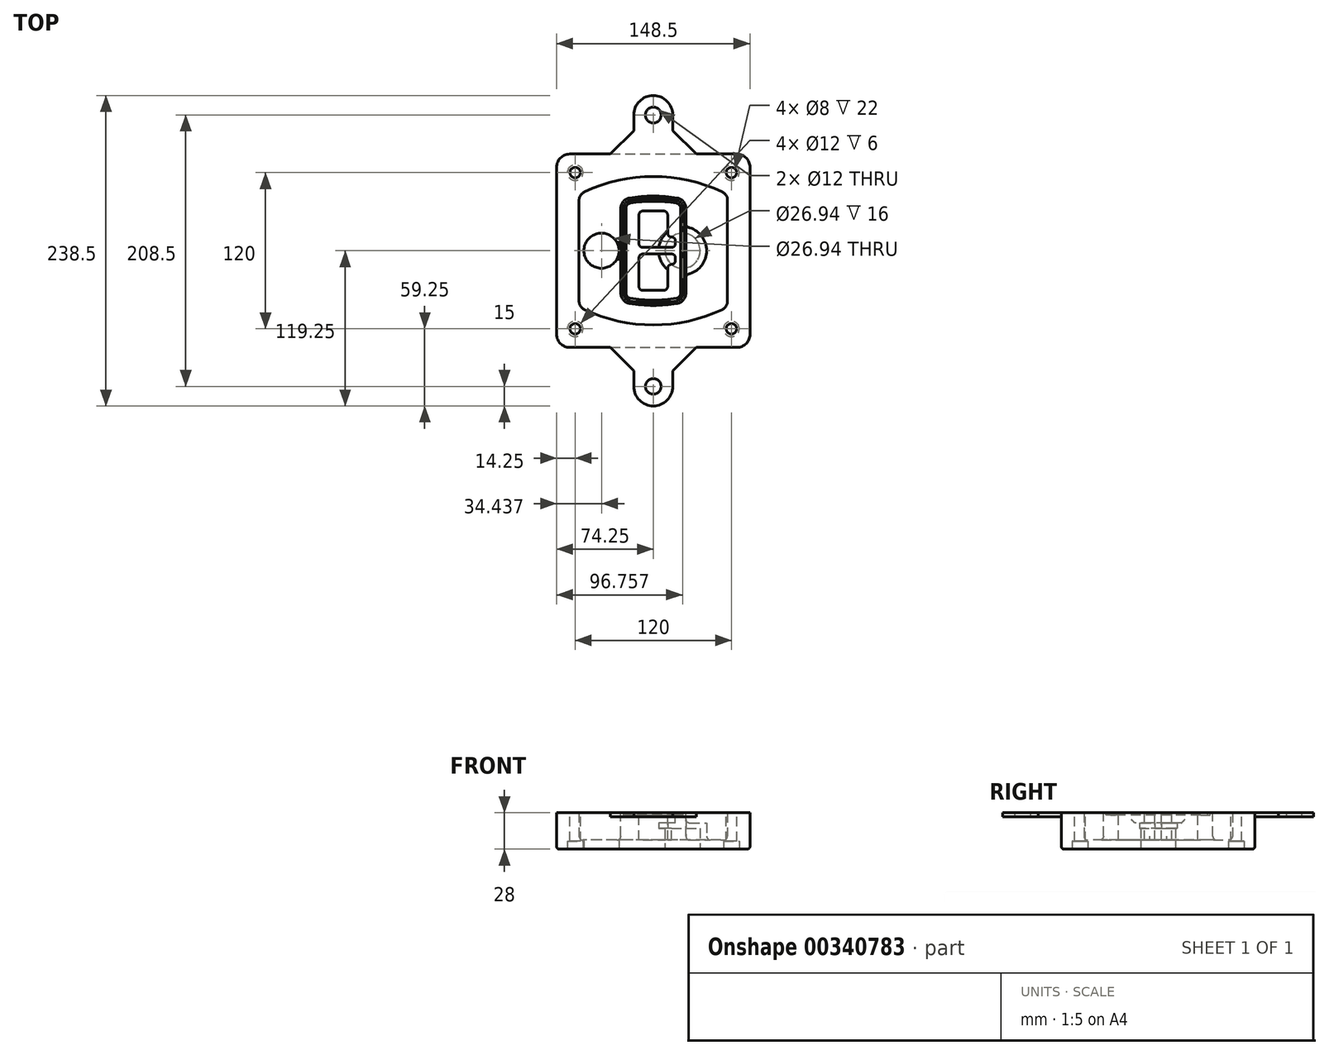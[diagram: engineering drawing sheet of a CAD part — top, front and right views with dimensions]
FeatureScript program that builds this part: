
annotation { "Feature Type Name" : "Feature", "Feature Type Description" : "" }
export const myFeature = defineFeature(function(context is Context, id is Id, definition is map)
    precondition{}
    {
        {
            var Q0;
            Q0=qCreatedBy(makeId("Top.planeOp"),FACE);
            var sketch = newSketch(context, id + "F0", { "sketchPlane" : qUnion([Q0])});
            skPoint(sketch, "E0.rect.middle", {"position": v(0, 0) * mm});
            skLineSegment(sketch, "E1.bottom", {"start": v(-64.25, -74.25) * mm, "end": v(64.25, -74.25) * mm});
            skLineSegment(sketch, "E1.top", {"start": v(-64.25, 74.25) * mm, "end": v(64.25, 74.25) * mm});
            skLineSegment(sketch, "E1.left", {"start": v(-74.25, -64.25) * mm, "end": v(-74.25, 64.25) * mm});
            skLineSegment(sketch, "E1.right", {"start": v(74.25, -64.25) * mm, "end": v(74.25, 64.25) * mm});
            skLineSegment(sketch, "E2", {"start": v(-74.25, 74.25) * mm, "end": v(74.25, -74.25) * mm, "construction": true});
            skLineSegment(sketch, "E3", {"start": v(74.25, 74.25) * mm, "end": v(-74.25, -74.25) * mm, "construction": true});
            skCircle(sketch, "E4", {"center": v(-60, 60) * mm, "radius": 4 * mm});
            skCircle(sketch, "E5", {"center": v(60, 60) * mm, "radius": 4 * mm});
            skCircle(sketch, "E6", {"center": v(60, -60) * mm, "radius": 4 * mm});
            skCircle(sketch, "E7", {"center": v(-60, -60) * mm, "radius": 4 * mm});
            skLineSegment(sketch, "E8", {"start": v(-60, 60) * mm, "end": v(60, 60) * mm, "construction": true});
            skLineSegment(sketch, "E9", {"start": v(60, 60) * mm, "end": v(60, -60) * mm, "construction": true});
            skLineSegment(sketch, "E10", {"start": v(60, -60) * mm, "end": v(-60, -60) * mm, "construction": true});
            skLineSegment(sketch, "E11", {"start": v(-60, -60) * mm, "end": v(-60, 60) * mm, "construction": true});
            skLineSegment(sketch, "E12", {"start": v(-60, 38.83) * mm, "end": v(-60, -38.83) * mm});
            skLineSegment(sketch, "E13", {"start": v(60, 38.83) * mm, "end": v(60, -38.83) * mm});
            skArc(sketch, "E14", {"start": v(54.26, 47.88) * mm, "mid": v(0, 60) * mm, "end": v(-54.26, 47.88) * mm});
            skArc(sketch, "E15", {"start": v(-54.26, -47.88) * mm, "mid": v(0, -60) * mm, "end": v(54.26, -47.88) * mm});
            skLineSegment(sketch, "E16", {"start": v(-60, 0) * mm, "end": v(60, 0) * mm, "construction": true});
            skPoint(sketch, "E17.visualSharp", {"position": v(-60, -45) * mm});
            skArc(sketch, "E17.filletArc", {"start": v(-60, -38.83) * mm, "mid": v(-58.44, -44.2) * mm, "end": v(-54.26, -47.88) * mm});
            skPoint(sketch, "E18.visualSharp", {"position": v(-60, 45) * mm});
            skArc(sketch, "E18.filletArc", {"start": v(-54.26, 47.88) * mm, "mid": v(-58.44, 44.2) * mm, "end": v(-60, 38.83) * mm});
            skPoint(sketch, "E19.visualSharp", {"position": v(60, 45) * mm});
            skArc(sketch, "E19.filletArc", {"start": v(60, 38.83) * mm, "mid": v(58.44, 44.2) * mm, "end": v(54.26, 47.88) * mm});
            skPoint(sketch, "E20.visualSharp", {"position": v(60, -45) * mm});
            skArc(sketch, "E20.filletArc", {"start": v(54.26, -47.88) * mm, "mid": v(58.44, -44.2) * mm, "end": v(60, -38.83) * mm});
            skPoint(sketch, "E21.visualSharp", {"position": v(-74.25, 74.25) * mm});
            skArc(sketch, "E21.filletArc", {"start": v(-64.25, 74.25) * mm, "mid": v(-71.32, 71.32) * mm, "end": v(-74.25, 64.25) * mm});
            skPoint(sketch, "E22.visualSharp", {"position": v(74.25, 74.25) * mm});
            skArc(sketch, "E22.filletArc", {"start": v(74.25, 64.25) * mm, "mid": v(71.32, 71.32) * mm, "end": v(64.25, 74.25) * mm});
            skPoint(sketch, "E23.visualSharp", {"position": v(74.25, -74.25) * mm});
            skArc(sketch, "E23.filletArc", {"start": v(64.25, -74.25) * mm, "mid": v(71.32, -71.32) * mm, "end": v(74.25, -64.25) * mm});
            skPoint(sketch, "E24.visualSharp", {"position": v(-74.25, -74.25) * mm});
            skArc(sketch, "E24.filletArc", {"start": v(-74.25, -64.25) * mm, "mid": v(-71.32, -71.32) * mm, "end": v(-64.25, -74.25) * mm});
            skArc(sketch, "E25.0", {"start": v(57, 38.83) * mm, "mid": v(55.9, 42.58) * mm, "end": v(52.98, 45.17) * mm});
            skLineSegment(sketch, "E25.1", {"start": v(57, 38.83) * mm, "end": v(57, -38.83) * mm});
            skArc(sketch, "E25.2", {"start": v(52.98, -45.17) * mm, "mid": v(55.9, -42.58) * mm, "end": v(57, -38.83) * mm});
            skArc(sketch, "E25.3", {"start": v(-52.98, -45.17) * mm, "mid": v(0, -57) * mm, "end": v(52.98, -45.17) * mm});
            skArc(sketch, "E25.4", {"start": v(-57, -38.83) * mm, "mid": v(-55.9, -42.58) * mm, "end": v(-52.98, -45.17) * mm});
            skArc(sketch, "E25.5", {"start": v(52.98, 45.17) * mm, "mid": v(0, 57) * mm, "end": v(-52.98, 45.17) * mm});
            skLineSegment(sketch, "E25.6", {"start": v(-57, 38.83) * mm, "end": v(-57, -38.83) * mm});
            skArc(sketch, "E25.7", {"start": v(-52.98, 45.17) * mm, "mid": v(-55.9, 42.58) * mm, "end": v(-57, 38.83) * mm});
            skArc(sketch, "E26.0", {"start": v(-55.96, 51.5) * mm, "mid": v(-61.82, 46.33) * mm, "end": v(-64, 38.83) * mm});
            skArc(sketch, "E26.1", {"start": v(55.96, 51.5) * mm, "mid": v(0, 64) * mm, "end": v(-55.96, 51.5) * mm});
            skArc(sketch, "E26.2", {"start": v(64, 38.83) * mm, "mid": v(61.82, 46.33) * mm, "end": v(55.96, 51.5) * mm});
            skLineSegment(sketch, "E26.3", {"start": v(64, 38.83) * mm, "end": v(64, -38.83) * mm});
            skArc(sketch, "E26.4", {"start": v(55.96, -51.5) * mm, "mid": v(61.82, -46.33) * mm, "end": v(64, -38.83) * mm});
            skLineSegment(sketch, "E26.5", {"start": v(-64, 38.83) * mm, "end": v(-64, -38.83) * mm});
            skArc(sketch, "E26.6", {"start": v(-55.96, -51.5) * mm, "mid": v(0, -64) * mm, "end": v(55.96, -51.5) * mm});
            skArc(sketch, "E26.7", {"start": v(-64, -38.83) * mm, "mid": v(-61.82, -46.33) * mm, "end": v(-55.96, -51.5) * mm});
            skSolve(sketch);
        }
        {
            var Q0;
            Q0=makeQuery(id+"F0.imprint","IMPRINT",FACE,{"disambiguationData":[TD([[makeQuery(id+"F0.imprint","IMPRINT",EDGE,{"derivedFrom":sQuery(id+"F0.wireOp",EDGE,"E1.bottom")}),1.0]])]});
            var Q1;
            Q1=makeQuery(id+"F0.imprint","IMPRINT",FACE,{"disambiguationData":[TD([[makeQuery(id+"F0.imprint","IMPRINT",EDGE,{"derivedFrom":sQuery(id+"F0.wireOp",EDGE,"E12")}),1.0]])]});
            var Q2;
            Q2=makeQuery(id+"F0.imprint","IMPRINT",FACE,{"disambiguationData":[TD([[makeQuery(id+"F0.imprint","IMPRINT",EDGE,{"derivedFrom":sQuery(id+"F0.wireOp",EDGE,"E25.0")}),1.0]])]});
            var Q3;
            Q3=makeQuery(id+"F0.imprint","IMPRINT",FACE,{"disambiguationData":[TD([[makeQuery(id+"F0.imprint","IMPRINT",EDGE,{"derivedFrom":sQuery(id+"F0.wireOp",EDGE,"E12")}),-1.0]])]});
            extrude(context, id + "F1", {"entities" : qUnion([Q0, Q1, Q2, Q3]), "oppositeDirection" : true, "depth" : 25 * mm});
        }
        {
            var Q0;
            Q0=makeQuery(id+"F0.imprint","IMPRINT",FACE,{"disambiguationData":[TD([[makeQuery(id+"F0.imprint","IMPRINT",EDGE,{"derivedFrom":sQuery(id+"F0.wireOp",EDGE,"E12")}),1.0]])]});
            extrude(context, id + "F2", {"entities" : qUnion([Q0]), "operationType" : NewBodyOperationType.ADD, "depth" : 3 * mm});
        }
        {
            var Q0;
            Q0=makeQuery(id+"F0.imprint","IMPRINT",FACE,{"disambiguationData":[TD([[makeQuery(id+"F0.imprint","IMPRINT",EDGE,{"derivedFrom":sQuery(id+"F0.wireOp",EDGE,"E25.0")}),1.0]])]});
            extrude(context, id + "F3", {"entities" : qUnion([Q0]), "operationType" : NewBodyOperationType.REMOVE, "oppositeDirection" : true, "depth" : 18 * mm});
        }
        {
            var Q0;
            Q0=makeQuery(id+"F2.opExtrude","CAP_FACE",FACE,{"disambiguationData":[OSD([sQuery(id+"F0.wireOp",EDGE,"E12"),sQuery(id+"F0.wireOp",EDGE,"E13"),sQuery(id+"F0.wireOp",EDGE,"E14"),sQuery(id+"F0.wireOp",EDGE,"E15"),sQuery(id+"F0.wireOp",EDGE,"E17.filletArc"),sQuery(id+"F0.wireOp",EDGE,"E18.filletArc"),sQuery(id+"F0.wireOp",EDGE,"E19.filletArc"),sQuery(id+"F0.wireOp",EDGE,"E20.filletArc"),sQuery(id+"F0.wireOp",EDGE,"E25.0"),sQuery(id+"F0.wireOp",EDGE,"E25.1"),sQuery(id+"F0.wireOp",EDGE,"E25.2"),sQuery(id+"F0.wireOp",EDGE,"E25.3"),sQuery(id+"F0.wireOp",EDGE,"E25.4"),sQuery(id+"F0.wireOp",EDGE,"E25.5"),sQuery(id+"F0.wireOp",EDGE,"E25.6"),sQuery(id+"F0.wireOp",EDGE,"E25.7")])],"isStart":false});
            var sketch = newSketch(context, id + "F4", { "sketchPlane" : qUnion([Q0])});
            skArc(sketch, "E27.0", {"start": v(-18.34, -40.45) * mm, "mid": v(0, -42) * mm, "end": v(18.34, -40.45) * mm});
            skArc(sketch, "E28.0", {"start": v(18.34, 40.45) * mm, "mid": v(0, 42) * mm, "end": v(-18.34, 40.45) * mm});
            skLineSegment(sketch, "E29", {"start": v(-25, 32.57) * mm, "end": v(-25, -32.57) * mm});
            skLineSegment(sketch, "E30", {"start": v(25, 32.57) * mm, "end": v(25, -32.57) * mm});
            skLineSegment(sketch, "E31", {"start": v(-25, 39.1) * mm, "end": v(25, 39.1) * mm, "construction": true});
            skLineSegment(sketch, "E32", {"start": v(-25, -39.1) * mm, "end": v(25, -39.1) * mm, "construction": true});
            skPoint(sketch, "E33.visualSharp", {"position": v(-25, 39.1) * mm});
            skArc(sketch, "E33.filletArc", {"start": v(-18.34, 40.45) * mm, "mid": v(-23.11, 37.73) * mm, "end": v(-25, 32.57) * mm});
            skPoint(sketch, "E34.visualSharp", {"position": v(25, 39.1) * mm});
            skArc(sketch, "E34.filletArc", {"start": v(25, 32.57) * mm, "mid": v(23.11, 37.73) * mm, "end": v(18.34, 40.45) * mm});
            skPoint(sketch, "E35.visualSharp", {"position": v(25, -39.1) * mm});
            skArc(sketch, "E35.filletArc", {"start": v(18.34, -40.45) * mm, "mid": v(23.11, -37.73) * mm, "end": v(25, -32.57) * mm});
            skPoint(sketch, "E36.visualSharp", {"position": v(-25, -39.1) * mm});
            skArc(sketch, "E36.filletArc", {"start": v(-25, -32.57) * mm, "mid": v(-23.11, -37.73) * mm, "end": v(-18.34, -40.45) * mm});
            skArc(sketch, "E37.0", {"start": v(52.98, 45.17) * mm, "mid": v(0, 57) * mm, "end": v(-52.98, 45.17) * mm});
            skArc(sketch, "E37.1", {"start": v(-52.98, 45.17) * mm, "mid": v(-55.9, 42.58) * mm, "end": v(-57, 38.83) * mm});
            skLineSegment(sketch, "E37.2", {"start": v(-57, 38.83) * mm, "end": v(-57, -38.83) * mm});
            skArc(sketch, "E37.3", {"start": v(-57, -38.83) * mm, "mid": v(-55.9, -42.58) * mm, "end": v(-52.98, -45.17) * mm});
            skArc(sketch, "E37.4", {"start": v(-52.98, -45.17) * mm, "mid": v(0, -57) * mm, "end": v(52.98, -45.17) * mm});
            skArc(sketch, "E37.5", {"start": v(52.98, -45.17) * mm, "mid": v(55.9, -42.58) * mm, "end": v(57, -38.83) * mm});
            skLineSegment(sketch, "E37.6", {"start": v(57, 38.83) * mm, "end": v(57, -38.83) * mm});
            skArc(sketch, "E37.7", {"start": v(57, 38.83) * mm, "mid": v(55.9, 42.58) * mm, "end": v(52.98, 45.17) * mm});
            skLineSegment(sketch, "E38.0", {"start": v(23, 32.57) * mm, "end": v(23, -32.57) * mm});
            skArc(sketch, "E38.1", {"start": v(18, -38.48) * mm, "mid": v(21.58, -36.44) * mm, "end": v(23, -32.57) * mm});
            skArc(sketch, "E38.2", {"start": v(-18, -38.48) * mm, "mid": v(0, -40) * mm, "end": v(18, -38.48) * mm});
            skArc(sketch, "E38.3", {"start": v(-23, -32.57) * mm, "mid": v(-21.58, -36.44) * mm, "end": v(-18, -38.48) * mm});
            skLineSegment(sketch, "E38.4", {"start": v(-23, 32.57) * mm, "end": v(-23, -32.57) * mm});
            skArc(sketch, "E38.5", {"start": v(23, 32.57) * mm, "mid": v(21.58, 36.44) * mm, "end": v(18, 38.48) * mm});
            skArc(sketch, "E38.6", {"start": v(-18, 38.48) * mm, "mid": v(-21.58, 36.44) * mm, "end": v(-23, 32.57) * mm});
            skArc(sketch, "E38.7", {"start": v(18, 38.48) * mm, "mid": v(0, 40) * mm, "end": v(-18, 38.48) * mm});
            skArc(sketch, "E39.0", {"start": v(21, 32.57) * mm, "mid": v(20.06, 35.15) * mm, "end": v(17.67, 36.5) * mm});
            skLineSegment(sketch, "E39.1", {"start": v(21, 32.57) * mm, "end": v(21, -32.57) * mm});
            skArc(sketch, "E39.2", {"start": v(17.67, -36.5) * mm, "mid": v(20.06, -35.15) * mm, "end": v(21, -32.57) * mm});
            skArc(sketch, "E39.3", {"start": v(-17.67, -36.5) * mm, "mid": v(0, -38) * mm, "end": v(17.67, -36.5) * mm});
            skArc(sketch, "E39.4", {"start": v(-21, -32.57) * mm, "mid": v(-20.06, -35.15) * mm, "end": v(-17.67, -36.5) * mm});
            skArc(sketch, "E39.5", {"start": v(17.67, 36.5) * mm, "mid": v(0, 38) * mm, "end": v(-17.67, 36.5) * mm});
            skLineSegment(sketch, "E39.6", {"start": v(-21, 32.57) * mm, "end": v(-21, -32.57) * mm});
            skArc(sketch, "E39.7", {"start": v(-17.67, 36.5) * mm, "mid": v(-20.06, 35.15) * mm, "end": v(-21, 32.57) * mm});
            skLineSegment(sketch, "E40", {"start": v(-25, 0) * mm, "end": v(25, 0) * mm, "construction": true});
            skLineSegment(sketch, "E41", {"start": v(-11, 5.5) * mm, "end": v(-11, 27.5) * mm});
            skLineSegment(sketch, "E42", {"start": v(-8, 30.5) * mm, "end": v(8, 30.5) * mm});
            skLineSegment(sketch, "E43", {"start": v(11, 27.5) * mm, "end": v(11, 13.5) * mm});
            skLineSegment(sketch, "E44", {"start": v(14, 10.5) * mm, "end": v(14, 10.5) * mm});
            skLineSegment(sketch, "E45", {"start": v(17, 7.5) * mm, "end": v(17, 5.5) * mm});
            skLineSegment(sketch, "E46", {"start": v(14, 2.5) * mm, "end": v(-8, 2.5) * mm});
            skPoint(sketch, "E47.visualSharp", {"position": v(-11, 30.5) * mm});
            skArc(sketch, "E47.filletArc", {"start": v(-8, 30.5) * mm, "mid": v(-10.12, 29.62) * mm, "end": v(-11, 27.5) * mm});
            skPoint(sketch, "E48.visualSharp", {"position": v(11, 30.5) * mm});
            skArc(sketch, "E48.filletArc", {"start": v(11, 27.5) * mm, "mid": v(10.12, 29.62) * mm, "end": v(8, 30.5) * mm});
            skPoint(sketch, "E49.visualSharp", {"position": v(11, 10.5) * mm});
            skArc(sketch, "E49.filletArc", {"start": v(11, 13.5) * mm, "mid": v(11.88, 11.38) * mm, "end": v(14, 10.5) * mm});
            skPoint(sketch, "E50.visualSharp", {"position": v(17, 10.5) * mm});
            skArc(sketch, "E50.filletArc", {"start": v(17, 7.5) * mm, "mid": v(16.12, 9.62) * mm, "end": v(14, 10.5) * mm});
            skPoint(sketch, "E51.visualSharp", {"position": v(17, 2.5) * mm});
            skArc(sketch, "E51.filletArc", {"start": v(14, 2.5) * mm, "mid": v(16.12, 3.38) * mm, "end": v(17, 5.5) * mm});
            skPoint(sketch, "E52.visualSharp", {"position": v(-11, 2.5) * mm});
            skArc(sketch, "E52.filletArc", {"start": v(-11, 5.5) * mm, "mid": v(-10.12, 3.38) * mm, "end": v(-8, 2.5) * mm});
            skLineSegment(sketch, "E53.0.MirrorCS", {"start": v(14, -2.5) * mm, "end": v(-8, -2.5) * mm});
            skArc(sketch, "E54.0.MirrorCS", {"start": v(-11, -5.5) * mm, "mid": v(-10.12, -3.38) * mm, "end": v(-8, -2.5) * mm});
            skLineSegment(sketch, "E55.0.MirrorCS", {"start": v(-11, -5.5) * mm, "end": v(-11, -27.5) * mm});
            skArc(sketch, "E56.0.MirrorCS", {"start": v(-8, -30.5) * mm, "mid": v(-10.12, -29.62) * mm, "end": v(-11, -27.5) * mm});
            skLineSegment(sketch, "E57.0.MirrorCS", {"start": v(-8, -30.5) * mm, "end": v(8, -30.5) * mm});
            skArc(sketch, "E58.0.MirrorCS", {"start": v(11, -27.5) * mm, "mid": v(10.12, -29.62) * mm, "end": v(8, -30.5) * mm});
            skLineSegment(sketch, "E59.0.MirrorCS", {"start": v(11, -27.5) * mm, "end": v(11, -13.5) * mm});
            skArc(sketch, "E60.0.MirrorCS", {"start": v(11, -13.5) * mm, "mid": v(11.88, -11.38) * mm, "end": v(14, -10.5) * mm});
            skArc(sketch, "E61.0.MirrorCS", {"start": v(17, -7.5) * mm, "mid": v(16.12, -9.62) * mm, "end": v(14, -10.5) * mm});
            skLineSegment(sketch, "E62.0.MirrorCS", {"start": v(17, -7.5) * mm, "end": v(17, -5.5) * mm});
            skArc(sketch, "E63.0.MirrorCS", {"start": v(14, -2.5) * mm, "mid": v(16.12, -3.38) * mm, "end": v(17, -5.5) * mm});
            skSolve(sketch);
        }
        {
            var Q0;
            Q0=makeQuery(id+"F4.imprint","IMPRINT",FACE,{"disambiguationData":[TD([[makeQuery(id+"F4.imprint","IMPRINT",EDGE,{"derivedFrom":sQuery(id+"F4.wireOp",EDGE,"E27.0")}),1.0]])]});
            var Q1;
            Q1=makeQuery(id+"F4.imprint","IMPRINT",FACE,{"disambiguationData":[TD([[makeQuery(id+"F4.imprint","IMPRINT",EDGE,{"derivedFrom":sQuery(id+"F4.wireOp",EDGE,"E38.0")}),-1.0]])]});
            var Q2;
            Q2=makeQuery(id+"F4.imprint","IMPRINT",FACE,{"disambiguationData":[TD([[makeQuery(id+"F4.imprint","IMPRINT",EDGE,{"derivedFrom":sQuery(id+"F4.wireOp",EDGE,"E39.0")}),1.0]])]});
            extrude(context, id + "F5", {"entities" : qUnion([Q0, Q1, Q2]), "operationType" : NewBodyOperationType.ADD, "endBound" : BoundingType.UP_TO_NEXT, "oppositeDirection" : true, "depth" : 25 * mm});
        }
        {
            var Q0;
            Q0=makeQuery(id+"F4.imprint","IMPRINT",FACE,{"disambiguationData":[TD([[makeQuery(id+"F4.imprint","IMPRINT",EDGE,{"derivedFrom":sQuery(id+"F4.wireOp",EDGE,"E38.0")}),-1.0]])]});
            extrude(context, id + "F6", {"entities" : qUnion([Q0]), "operationType" : NewBodyOperationType.REMOVE, "oppositeDirection" : true, "depth" : 2 * mm});
        }
        {
            var Q0;
            Q0=makeQuery(id+"F1.opExtrude","CAP_FACE",FACE,{"disambiguationData":[OSD([sQuery(id+"F0.wireOp",EDGE,"E1.bottom"),sQuery(id+"F0.wireOp",EDGE,"E1.top"),sQuery(id+"F0.wireOp",EDGE,"E1.left"),sQuery(id+"F0.wireOp",EDGE,"E1.right"),sQuery(id+"F0.wireOp",EDGE,"E4"),sQuery(id+"F0.wireOp",EDGE,"E5"),sQuery(id+"F0.wireOp",EDGE,"E6"),sQuery(id+"F0.wireOp",EDGE,"E7"),sQuery(id+"F0.wireOp",EDGE,"E21.filletArc"),sQuery(id+"F0.wireOp",EDGE,"E22.filletArc"),sQuery(id+"F0.wireOp",EDGE,"E23.filletArc"),sQuery(id+"F0.wireOp",EDGE,"E24.filletArc")])],"isStart":false});
            var sketch = newSketch(context, id + "F7", { "sketchPlane" : qUnion([Q0])});
            skCircle(sketch, "E64", {"center": v(22.5, 0) * mm, "radius": 13.47 * mm});
            skCircle(sketch, "E65", {"center": v(-39.81, 0) * mm, "radius": 13.47 * mm});
            skLineSegment(sketch, "E66", {"start": v(74.25, 0) * mm, "end": v(-74.25, 0) * mm});
            skCircle(sketch, "E67", {"center": v(22.5, 0) * mm, "radius": 18.47 * mm});
            skCircle(sketch, "E68", {"center": v(60, -60) * mm, "radius": 6 * mm});
            skCircle(sketch, "E69", {"center": v(-60, -60) * mm, "radius": 6 * mm});
            skCircle(sketch, "E70", {"center": v(-60, 60) * mm, "radius": 6 * mm});
            skCircle(sketch, "E71", {"center": v(60, 60) * mm, "radius": 6 * mm});
            skSolve(sketch);
        }
        {
            var Q0;
            {var subQ1=sQuery(id+"F7.wireOp",EDGE,"E66");var subQ4=sQuery(id+"F7.wireOp",EDGE,"E64");var subQ6=makeQuery(id+"F7.imprint","INTERSECT",VERTEX,{"disambiguationData":[OD(0.0)],"derivedFrom":[subQ4,subQ1]});Q0=makeQuery(id+"F7.imprint","IMPRINT",FACE,{"disambiguationData":[TD([[makeQuery(id+"F7.imprint","IMPRINT",EDGE,{"disambiguationData":[TD([[subQ6,-1.0]])],"derivedFrom":subQ4}),-1.0]])]});}
            var Q1;
            {var subQ0=sQuery(id+"F7.wireOp",EDGE,"E66");var subQ1=sQuery(id+"F7.wireOp",EDGE,"E64");var subQ3=makeQuery(id+"F7.imprint","INTERSECT",VERTEX,{"disambiguationData":[OD(0.0)],"derivedFrom":[subQ1,subQ0]});Q1=makeQuery(id+"F7.imprint","IMPRINT",FACE,{"disambiguationData":[TD([[makeQuery(id+"F7.imprint","IMPRINT",EDGE,{"disambiguationData":[TD([[subQ3,-1.0]])],"derivedFrom":subQ1}),1.0]])]});}
            var Q2;
            {var subQ0=sQuery(id+"F7.wireOp",EDGE,"E66");var subQ1=sQuery(id+"F7.wireOp",EDGE,"E64");var subQ3=makeQuery(id+"F7.imprint","INTERSECT",VERTEX,{"disambiguationData":[OD(0.0)],"derivedFrom":[subQ1,subQ0]});Q2=makeQuery(id+"F7.imprint","IMPRINT",FACE,{"disambiguationData":[TD([[makeQuery(id+"F7.imprint","IMPRINT",EDGE,{"disambiguationData":[TD([[subQ3,1.0]])],"derivedFrom":subQ1}),1.0]])]});}
            var Q3;
            {var subQ1=sQuery(id+"F7.wireOp",EDGE,"E66");var subQ4=sQuery(id+"F7.wireOp",EDGE,"E64");var subQ6=makeQuery(id+"F7.imprint","INTERSECT",VERTEX,{"disambiguationData":[OD(0.0)],"derivedFrom":[subQ4,subQ1]});Q3=makeQuery(id+"F7.imprint","IMPRINT",FACE,{"disambiguationData":[TD([[makeQuery(id+"F7.imprint","IMPRINT",EDGE,{"disambiguationData":[TD([[subQ6,1.0]])],"derivedFrom":subQ4}),-1.0]])]});}
            extrude(context, id + "F8", {"entities" : qUnion([Q0, Q1, Q2, Q3]), "operationType" : NewBodyOperationType.ADD, "oppositeDirection" : true, "depth" : 20 * mm});
        }
        {
            var Q0;
            {var subQ0=sQuery(id+"F7.wireOp",EDGE,"E66");var subQ1=sQuery(id+"F7.wireOp",EDGE,"E64");var subQ3=makeQuery(id+"F7.imprint","INTERSECT",VERTEX,{"disambiguationData":[OD(0.0)],"derivedFrom":[subQ1,subQ0]});Q0=makeQuery(id+"F7.imprint","IMPRINT",FACE,{"disambiguationData":[TD([[makeQuery(id+"F7.imprint","IMPRINT",EDGE,{"disambiguationData":[TD([[subQ3,-1.0]])],"derivedFrom":subQ1}),1.0]])]});}
            var Q1;
            {var subQ0=sQuery(id+"F7.wireOp",EDGE,"E66");var subQ1=sQuery(id+"F7.wireOp",EDGE,"E64");var subQ3=makeQuery(id+"F7.imprint","INTERSECT",VERTEX,{"disambiguationData":[OD(0.0)],"derivedFrom":[subQ1,subQ0]});Q1=makeQuery(id+"F7.imprint","IMPRINT",FACE,{"disambiguationData":[TD([[makeQuery(id+"F7.imprint","IMPRINT",EDGE,{"disambiguationData":[TD([[subQ3,1.0]])],"derivedFrom":subQ1}),1.0]])]});}
            extrude(context, id + "F9", {"entities" : qUnion([Q0, Q1]), "operationType" : NewBodyOperationType.REMOVE, "oppositeDirection" : true, "depth" : 16 * mm});
        }
        {
            var Q0;
            {var subQ0=sQuery(id+"F7.wireOp",EDGE,"E66");var subQ1=sQuery(id+"F7.wireOp",EDGE,"E65");var subQ3=makeQuery(id+"F7.imprint","INTERSECT",VERTEX,{"disambiguationData":[OD(0.0)],"derivedFrom":[subQ1,subQ0]});Q0=makeQuery(id+"F7.imprint","IMPRINT",FACE,{"disambiguationData":[TD([[makeQuery(id+"F7.imprint","IMPRINT",EDGE,{"disambiguationData":[TD([[subQ3,-1.0]])],"derivedFrom":subQ1}),1.0]])]});}
            var Q1;
            {var subQ0=sQuery(id+"F7.wireOp",EDGE,"E66");var subQ1=sQuery(id+"F7.wireOp",EDGE,"E65");var subQ3=makeQuery(id+"F7.imprint","INTERSECT",VERTEX,{"disambiguationData":[OD(0.0)],"derivedFrom":[subQ1,subQ0]});Q1=makeQuery(id+"F7.imprint","IMPRINT",FACE,{"disambiguationData":[TD([[makeQuery(id+"F7.imprint","IMPRINT",EDGE,{"disambiguationData":[TD([[subQ3,1.0]])],"derivedFrom":subQ1}),1.0]])]});}
            extrude(context, id + "F10", {"entities" : qUnion([Q0, Q1]), "operationType" : NewBodyOperationType.REMOVE, "oppositeDirection" : true, "depth" : 25 * mm});
        }
        {
            var Q0;
            Q0=makeQuery(id+"F7.imprint","IMPRINT",FACE,{"disambiguationData":[TD([[makeQuery(id+"F7.imprint","IMPRINT",EDGE,{"derivedFrom":sQuery(id+"F7.wireOp",EDGE,"E68")}),1.0]])]});
            var Q1;
            Q1=makeQuery(id+"F7.imprint","IMPRINT",FACE,{"disambiguationData":[TD([[makeQuery(id+"F7.imprint","IMPRINT",EDGE,{"derivedFrom":makeQuery(id+"F1.opExtrude","CAP_EDGE",EDGE,{"disambiguationData":[OSD([sQuery(id+"F0.wireOp",EDGE,"E5")])],"isStart":false})}),-1.0]])]});
            var Q2;
            Q2=makeQuery(id+"F7.imprint","IMPRINT",FACE,{"disambiguationData":[TD([[makeQuery(id+"F7.imprint","IMPRINT",EDGE,{"derivedFrom":sQuery(id+"F7.wireOp",EDGE,"E69")}),1.0]])]});
            var Q3;
            Q3=makeQuery(id+"F7.imprint","IMPRINT",FACE,{"disambiguationData":[TD([[makeQuery(id+"F7.imprint","IMPRINT",EDGE,{"derivedFrom":makeQuery(id+"F1.opExtrude","CAP_EDGE",EDGE,{"disambiguationData":[OSD([sQuery(id+"F0.wireOp",EDGE,"E4")])],"isStart":false})}),-1.0]])]});
            var Q4;
            Q4=makeQuery(id+"F7.imprint","IMPRINT",FACE,{"disambiguationData":[TD([[makeQuery(id+"F7.imprint","IMPRINT",EDGE,{"derivedFrom":sQuery(id+"F7.wireOp",EDGE,"E70")}),1.0]])]});
            var Q5;
            Q5=makeQuery(id+"F7.imprint","IMPRINT",FACE,{"disambiguationData":[TD([[makeQuery(id+"F7.imprint","IMPRINT",EDGE,{"derivedFrom":makeQuery(id+"F1.opExtrude","CAP_EDGE",EDGE,{"disambiguationData":[OSD([sQuery(id+"F0.wireOp",EDGE,"E7")])],"isStart":false})}),-1.0]])]});
            var Q6;
            Q6=makeQuery(id+"F7.imprint","IMPRINT",FACE,{"disambiguationData":[TD([[makeQuery(id+"F7.imprint","IMPRINT",EDGE,{"derivedFrom":sQuery(id+"F7.wireOp",EDGE,"E71")}),1.0]])]});
            var Q7;
            Q7=makeQuery(id+"F7.imprint","IMPRINT",FACE,{"disambiguationData":[TD([[makeQuery(id+"F7.imprint","IMPRINT",EDGE,{"derivedFrom":makeQuery(id+"F1.opExtrude","CAP_EDGE",EDGE,{"disambiguationData":[OSD([sQuery(id+"F0.wireOp",EDGE,"E6")])],"isStart":false})}),-1.0]])]});
            extrude(context, id + "F11", {"entities" : qUnion([Q0, Q1, Q2, Q3, Q4, Q5, Q6, Q7]), "operationType" : NewBodyOperationType.REMOVE, "oppositeDirection" : true, "depth" : 6 * mm});
        }
        {
            var Q0;
            Q0=makeQuery(id+"F9.boolean.opBoolean","COPY",FACE,{"derivedFrom":makeQuery(id+"F9.opExtrude","CAP_FACE",FACE,{"disambiguationData":[OSD([sQuery(id+"F7.wireOp",EDGE,"E64")])],"isStart":false})});
            var sketch = newSketch(context, id + "F12", { "sketchPlane" : qUnion([Q0])});
            skArc(sketch, "E72.0", {"start": v(11, 14.45) * mm, "mid": v(6.45, 9.13) * mm, "end": v(4.2, 2.5) * mm});
            skArc(sketch, "E72.1", {"start": v(4.2, -2.5) * mm, "mid": v(6.45, -9.13) * mm, "end": v(11, -14.45) * mm});
            skLineSegment(sketch, "E73", {"start": v(4.2, -2.5) * mm, "end": v(14, -2.5) * mm});
            skLineSegment(sketch, "E74.0", {"start": v(14, 2.5) * mm, "end": v(4.2, 2.5) * mm});
            skArc(sketch, "E74.1", {"start": v(14, 2.5) * mm, "mid": v(16.12, 3.38) * mm, "end": v(17, 5.5) * mm});
            skLineSegment(sketch, "E74.2", {"start": v(17, 7.5) * mm, "end": v(17, 5.5) * mm});
            skArc(sketch, "E74.3", {"start": v(17, 7.5) * mm, "mid": v(16.12, 9.62) * mm, "end": v(14, 10.5) * mm});
            skArc(sketch, "E74.4", {"start": v(11, 13.5) * mm, "mid": v(11.88, 11.38) * mm, "end": v(14, 10.5) * mm});
            skLineSegment(sketch, "E74.5", {"start": v(11, 14.45) * mm, "end": v(11, 13.5) * mm});
            skLineSegment(sketch, "E74.7", {"start": v(14, -2.5) * mm, "end": v(4.2, -2.5) * mm});
            skArc(sketch, "E74.8", {"start": v(14, -2.5) * mm, "mid": v(16.12, -3.38) * mm, "end": v(17, -5.5) * mm});
            skLineSegment(sketch, "E74.9", {"start": v(17, -7.5) * mm, "end": v(17, -5.5) * mm});
            skArc(sketch, "E74.10", {"start": v(17, -7.5) * mm, "mid": v(16.12, -9.62) * mm, "end": v(14, -10.5) * mm});
            skArc(sketch, "E74.11", {"start": v(11, -13.5) * mm, "mid": v(11.88, -11.38) * mm, "end": v(14, -10.5) * mm});
            skLineSegment(sketch, "E74.12", {"start": v(11, -14.45) * mm, "end": v(11, -13.5) * mm});
            skPoint(sketch, "E75.orphan", {"position": v(11, -27.5) * mm});
            skPoint(sketch, "E76.orphan", {"position": v(-8, -2.5) * mm});
            skPoint(sketch, "E77.orphan", {"position": v(-8, 2.5) * mm});
            skPoint(sketch, "E78.orphan", {"position": v(11, 27.5) * mm});
            skSolve(sketch);
        }
        {
            var Q0;
            {var subQ7=sQuery(id+"F12.wireOp",EDGE,"E72.0");var subQ14=sQuery(id+"F12.wireOp",EDGE,"E72.1");var subQ16=sQuery(id+"F12.wireOp",EDGE,"E74.1");var subQ18=sQuery(id+"F12.wireOp",EDGE,"E74.8");Q0=qUnion([makeQuery(id+"F12.imprint","IMPRINT",FACE,{"disambiguationData":[TD([[makeQuery(id+"F12.imprint","IMPRINT",EDGE,{"derivedFrom":subQ7}),1.0]])]}),makeQuery(id+"F12.imprint","IMPRINT",FACE,{"disambiguationData":[TD([[makeQuery(id+"F12.imprint","IMPRINT",EDGE,{"derivedFrom":subQ14}),1.0]])]}),makeQuery(id+"F12.imprint","IMPRINT",FACE,{"disambiguationData":[TD([[makeQuery(id+"F12.imprint","IMPRINT",EDGE,{"derivedFrom":subQ16}),1.0]])]}),makeQuery(id+"F12.imprint","IMPRINT",FACE,{"disambiguationData":[TD([[makeQuery(id+"F12.imprint","IMPRINT",EDGE,{"derivedFrom":subQ18}),-1.0]])]})]);}
            var Q1;
            Q1=makeQuery(id+"F5.boolean.opBoolean","SPLIT",FACE,{"disambiguationData":[TD([makeQuery(id+"F5.opExtrude","SWEPT_FACE",FACE,{"disambiguationData":[OSD([sQuery(id+"F4.wireOp",EDGE,"E41")])]})])],"derivedFrom":makeQuery(id+"F3.boolean.opBoolean","COPY",FACE,{"derivedFrom":makeQuery(id+"F3.opExtrude","CAP_FACE",FACE,{"disambiguationData":[OSD([sQuery(id+"F0.wireOp",EDGE,"E25.0"),sQuery(id+"F0.wireOp",EDGE,"E25.1"),sQuery(id+"F0.wireOp",EDGE,"E25.2"),sQuery(id+"F0.wireOp",EDGE,"E25.3"),sQuery(id+"F0.wireOp",EDGE,"E25.4"),sQuery(id+"F0.wireOp",EDGE,"E25.5"),sQuery(id+"F0.wireOp",EDGE,"E25.6"),sQuery(id+"F0.wireOp",EDGE,"E25.7")])],"isStart":false})})});
            extrude(context, id + "F13", {"entities" : qUnion([Q0]), "operationType" : NewBodyOperationType.REMOVE, "endBound" : BoundingType.UP_TO_SURFACE, "endBoundEntityFace" : qUnion([Q1]), "depth" : 25 * mm});
        }
        {
            var Q0;
            Q0=makeQuery(id+"F3.boolean.opBoolean","COPY",EDGE,{"derivedFrom":makeQuery(id+"F3.opExtrude","CAP_EDGE",EDGE,{"disambiguationData":[OSD([sQuery(id+"F0.wireOp",EDGE,"E25.6")])],"isStart":false})});
            var Q1;
            Q1=makeQuery(id+"F8.boolean.opBoolean","INTERSECT",EDGE,{"derivedFrom":[makeQuery(id+"F5.opExtrude","SWEPT_FACE",FACE,{"disambiguationData":[OSD([sQuery(id+"F4.wireOp",EDGE,"E30")])]}),makeQuery(id+"F8.opExtrude","CAP_FACE",FACE,{"disambiguationData":[OSD([sQuery(id+"F7.wireOp",EDGE,"E67")])],"isStart":false})]});
            var Q2;
            Q2=makeQuery(id+"F8.boolean.opBoolean","INTERSECT",EDGE,{"disambiguationData":[OD(1.0)],"derivedFrom":[makeQuery(id+"F5.opExtrude","SWEPT_FACE",FACE,{"disambiguationData":[OSD([sQuery(id+"F4.wireOp",EDGE,"E30")])]}),makeQuery(id+"F8.opExtrude","SWEPT_FACE",FACE,{"disambiguationData":[OSD([sQuery(id+"F7.wireOp",EDGE,"E67")])]})]});
            var Q3;
            {var subQ0=sQuery(id+"F4.wireOp",EDGE,"E30");Q3=makeQuery(id+"F8.boolean.opBoolean","SPLIT",EDGE,{"disambiguationData":[TD([makeQuery(id+"F5.opExtrude","SWEPT_FACE",FACE,{"disambiguationData":[OSD([sQuery(id+"F4.wireOp",EDGE,"E35.filletArc")])]})])],"derivedFrom":makeQuery(id+"F5.opExtrude","CAP_EDGE",EDGE,{"disambiguationData":[OSD([subQ0])],"isStart":false})});}
            var Q4;
            {var subQ0=sQuery(id+"F0.wireOp",EDGE,"E25.7");var subQ1=sQuery(id+"F0.wireOp",EDGE,"E25.1");var subQ2=sQuery(id+"F0.wireOp",EDGE,"E25.6");var subQ3=sQuery(id+"F0.wireOp",EDGE,"E25.5");var subQ4=sQuery(id+"F0.wireOp",EDGE,"E25.4");var subQ5=sQuery(id+"F0.wireOp",EDGE,"E25.0");var subQ6=sQuery(id+"F0.wireOp",EDGE,"E25.2");var subQ7=sQuery(id+"F0.wireOp",EDGE,"E25.3");Q4=makeQuery(id+"F8.boolean.opBoolean","INTERSECT",EDGE,{"derivedFrom":[makeQuery(id+"F5.boolean.opBoolean","SPLIT",FACE,{"disambiguationData":[TD([makeQuery(id+"F2.opExtrude","SWEPT_FACE",FACE,{"disambiguationData":[OSD([subQ5])]})])],"derivedFrom":makeQuery(id+"F3.boolean.opBoolean","COPY",FACE,{"derivedFrom":makeQuery(id+"F3.opExtrude","CAP_FACE",FACE,{"disambiguationData":[OSD([subQ5,subQ1,subQ6,subQ7,subQ4,subQ3,subQ2,subQ0])],"isStart":false})})}),makeQuery(id+"F8.opExtrude","SWEPT_FACE",FACE,{"disambiguationData":[OSD([sQuery(id+"F7.wireOp",EDGE,"E67")])]})]});}
            var Q5;
            Q5=makeQuery(id+"F8.boolean.opBoolean","INTERSECT",EDGE,{"disambiguationData":[OD(0.0)],"derivedFrom":[makeQuery(id+"F5.opExtrude","SWEPT_FACE",FACE,{"disambiguationData":[OSD([sQuery(id+"F4.wireOp",EDGE,"E30")])]}),makeQuery(id+"F8.opExtrude","SWEPT_FACE",FACE,{"disambiguationData":[OSD([sQuery(id+"F7.wireOp",EDGE,"E67")])]})]});
            fillet(context, id + "F14", {"entities" : qUnion([Q0, Q1, Q2, Q3, Q4, Q5]), "radius" : 3 * mm, "tangentPropagation" : true, "allowEdgeOverflow" : false});
        }
        {
            var Q0;
            Q0=makeQuery(id+"F1.opExtrude","CAP_EDGE",EDGE,{"disambiguationData":[OSD([sQuery(id+"F0.wireOp",EDGE,"E1.bottom")])],"isStart":false});
            fillet(context, id + "F15", {"entities" : qUnion([Q0]), "radius" : 2 * mm, "tangentPropagation" : true, "allowEdgeOverflow" : false});
        }
        {
            var Q0;
            {var subQ0=sQuery(id+"F0.wireOp",EDGE,"E21.filletArc");var subQ1=sQuery(id+"F0.wireOp",EDGE,"E7");var subQ2=sQuery(id+"F0.wireOp",EDGE,"E6");var subQ3=sQuery(id+"F0.wireOp",EDGE,"E5");var subQ4=sQuery(id+"F0.wireOp",EDGE,"E4");var subQ5=sQuery(id+"F0.wireOp",EDGE,"E22.filletArc");var subQ6=sQuery(id+"F0.wireOp",EDGE,"E1.bottom");var subQ7=sQuery(id+"F0.wireOp",EDGE,"E1.right");var subQ8=sQuery(id+"F0.wireOp",EDGE,"E1.top");var subQ9=sQuery(id+"F0.wireOp",EDGE,"E1.left");var subQ10=sQuery(id+"F0.wireOp",EDGE,"E23.filletArc");var subQ11=sQuery(id+"F0.wireOp",EDGE,"E24.filletArc");Q0=makeQuery(id+"F2.boolean.opBoolean","SPLIT",FACE,{"disambiguationData":[TD([makeQuery(id+"F1.opExtrude","SWEPT_FACE",FACE,{"disambiguationData":[OSD([subQ6])]})])],"derivedFrom":makeQuery(id+"F1.opExtrude","CAP_FACE",FACE,{"disambiguationData":[OSD([subQ6,subQ8,subQ9,subQ7,subQ4,subQ3,subQ2,subQ1,subQ0,subQ5,subQ10,subQ11])],"isStart":true})});}
            var sketch = newSketch(context, id + "F16", { "sketchPlane" : qUnion([Q0])});
            skArc(sketch, "E79.0", {"start": v(-64.25, 74.25) * mm, "mid": v(-71.32, 71.32) * mm, "end": v(-74.25, 64.25) * mm});
            skLineSegment(sketch, "E79.1", {"start": v(-64.25, 74.25) * mm, "end": v(64.25, 74.25) * mm});
            skLineSegment(sketch, "E79.2", {"start": v(-74.25, -64.25) * mm, "end": v(-74.25, 64.25) * mm});
            skArc(sketch, "E79.3", {"start": v(-74.25, -64.25) * mm, "mid": v(-71.32, -71.32) * mm, "end": v(-64.25, -74.25) * mm});
            skLineSegment(sketch, "E79.4", {"start": v(-64.25, -74.25) * mm, "end": v(64.25, -74.25) * mm});
            skArc(sketch, "E79.5", {"start": v(64.25, -74.25) * mm, "mid": v(71.32, -71.32) * mm, "end": v(74.25, -64.25) * mm});
            skLineSegment(sketch, "E79.6", {"start": v(74.25, -64.25) * mm, "end": v(74.25, 64.25) * mm});
            skArc(sketch, "E79.7", {"start": v(74.25, 64.25) * mm, "mid": v(71.32, 71.32) * mm, "end": v(64.25, 74.25) * mm});
            skArc(sketch, "E79.8", {"start": v(60, 38.83) * mm, "mid": v(58.44, 44.2) * mm, "end": v(54.26, 47.88) * mm});
            skLineSegment(sketch, "E79.9", {"start": v(60, 38.83) * mm, "end": v(60, -38.83) * mm});
            skArc(sketch, "E79.10", {"start": v(-54.26, -47.88) * mm, "mid": v(0, -60) * mm, "end": v(54.26, -47.88) * mm});
            skLineSegment(sketch, "E79.11", {"start": v(-60, 38.83) * mm, "end": v(-60, -38.83) * mm});
            skArc(sketch, "E79.12", {"start": v(54.26, 47.88) * mm, "mid": v(0, 60) * mm, "end": v(-54.26, 47.88) * mm});
            skArc(sketch, "E79.13", {"start": v(-54.26, 47.88) * mm, "mid": v(-58.44, 44.2) * mm, "end": v(-60, 38.83) * mm});
            skArc(sketch, "E79.14", {"start": v(-60, -38.83) * mm, "mid": v(-58.44, -44.2) * mm, "end": v(-54.26, -47.88) * mm});
            skArc(sketch, "E79.15", {"start": v(54.26, -47.88) * mm, "mid": v(58.44, -44.2) * mm, "end": v(60, -38.83) * mm});
            skCircle(sketch, "E79.16", {"center": v(60, 60) * mm, "radius": 4 * mm});
            skCircle(sketch, "E79.17", {"center": v(-60, 60) * mm, "radius": 4 * mm});
            skCircle(sketch, "E79.18", {"center": v(-60, -60) * mm, "radius": 4 * mm});
            skCircle(sketch, "E79.19", {"center": v(60, -60) * mm, "radius": 4 * mm});
            skLineSegment(sketch, "E80", {"start": v(-33, 74.25) * mm, "end": v(-15, 92.25) * mm});
            skLineSegment(sketch, "E81", {"start": v(-15, 92.25) * mm, "end": v(-15, 104.25) * mm});
            skLineSegment(sketch, "E82", {"start": v(33, 74.25) * mm, "end": v(15, 92.25) * mm});
            skLineSegment(sketch, "E83", {"start": v(15, 92.25) * mm, "end": v(15, 104.25) * mm});
            skLineSegment(sketch, "E84", {"start": v(0, 74.25) * mm, "end": v(0, 104.25) * mm, "construction": true});
            skCircle(sketch, "E85", {"center": v(0, 104.25) * mm, "radius": 6 * mm});
            skArc(sketch, "E86", {"start": v(-15, 104.25) * mm, "mid": v(0, 119.25) * mm, "end": v(15, 104.25) * mm});
            skLineSegment(sketch, "E87", {"start": v(-74.25, 0) * mm, "end": v(74.25, 0) * mm, "construction": true});
            skLineSegment(sketch, "E88.MirrorCS", {"start": v(-33, -74.25) * mm, "end": v(-15, -92.25) * mm});
            skLineSegment(sketch, "E89.MirrorCS", {"start": v(-15, -92.25) * mm, "end": v(-15, -104.25) * mm});
            skArc(sketch, "E90.MirrorCS", {"start": v(-15, -104.25) * mm, "mid": v(0, -119.25) * mm, "end": v(15, -104.25) * mm});
            skLineSegment(sketch, "E91.MirrorCS", {"start": v(15, -92.25) * mm, "end": v(15, -104.25) * mm});
            skLineSegment(sketch, "E92.MirrorCS", {"start": v(33, -74.25) * mm, "end": v(15, -92.25) * mm});
            skLineSegment(sketch, "E93.MirrorCS", {"start": v(0, -74.25) * mm, "end": v(0, -104.25) * mm, "construction": true});
            skCircle(sketch, "E94.MirrorC", {"center": v(0, -104.25) * mm, "radius": 6 * mm});
            skSolve(sketch);
        }
        {
            var Q0;
            {var subQ1=sQuery(id+"F16.wireOp",EDGE,"E80");Q0=makeQuery(id+"F16.imprint","IMPRINT",FACE,{"disambiguationData":[TD([[makeQuery(id+"F16.imprint","IMPRINT",EDGE,{"derivedFrom":subQ1}),-1.0]])]});}
            var Q1;
            {var subQ4=sQuery(id+"F16.wireOp",EDGE,"E79.0");Q1=makeQuery(id+"F16.imprint","IMPRINT",FACE,{"disambiguationData":[TD([[makeQuery(id+"F16.imprint","IMPRINT",EDGE,{"derivedFrom":subQ4}),1.0]])]});}
            var Q2;
            {var subQ0=sQuery(id+"F16.wireOp",EDGE,"E88.MirrorCS");Q2=makeQuery(id+"F16.imprint","IMPRINT",FACE,{"disambiguationData":[TD([[makeQuery(id+"F16.imprint","IMPRINT",EDGE,{"derivedFrom":subQ0}),1.0]])]});}
            var Q3;
            Q3=makeQuery(id+"F2.opExtrude","CAP_FACE",FACE,{"disambiguationData":[OSD([sQuery(id+"F0.wireOp",EDGE,"E12"),sQuery(id+"F0.wireOp",EDGE,"E13"),sQuery(id+"F0.wireOp",EDGE,"E14"),sQuery(id+"F0.wireOp",EDGE,"E15"),sQuery(id+"F0.wireOp",EDGE,"E17.filletArc"),sQuery(id+"F0.wireOp",EDGE,"E18.filletArc"),sQuery(id+"F0.wireOp",EDGE,"E19.filletArc"),sQuery(id+"F0.wireOp",EDGE,"E20.filletArc"),sQuery(id+"F0.wireOp",EDGE,"E25.0"),sQuery(id+"F0.wireOp",EDGE,"E25.1"),sQuery(id+"F0.wireOp",EDGE,"E25.2"),sQuery(id+"F0.wireOp",EDGE,"E25.3"),sQuery(id+"F0.wireOp",EDGE,"E25.4"),sQuery(id+"F0.wireOp",EDGE,"E25.5"),sQuery(id+"F0.wireOp",EDGE,"E25.6"),sQuery(id+"F0.wireOp",EDGE,"E25.7")])],"isStart":false});
            extrude(context, id + "F17", {"entities" : qUnion([Q0, Q1, Q2]), "operationType" : NewBodyOperationType.ADD, "endBound" : BoundingType.UP_TO_SURFACE, "endBoundEntityFace" : qUnion([Q3]), "depth" : 25 * mm});
        }
    });
